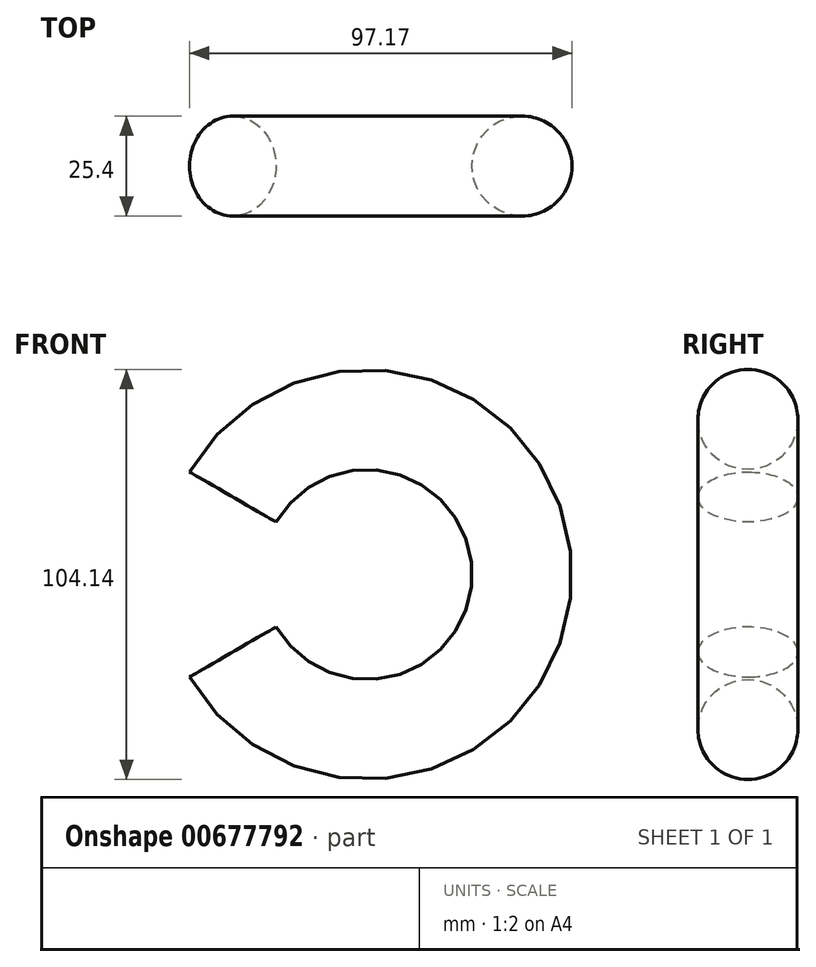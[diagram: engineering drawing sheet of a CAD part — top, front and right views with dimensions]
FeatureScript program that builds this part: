
annotation { "Feature Type Name" : "Feature", "Feature Type Description" : "" }
export const myFeature = defineFeature(function(context is Context, id is Id, definition is map)
    precondition{}
    {
        {
            var Q0;
            Q0=qCreatedBy(makeId("Top.planeOp"),FACE);
            var sketch = newSketch(context, id + "F0", { "sketchPlane" : qUnion([Q0])});
            skLineSegment(sketch, "E0", {"start": v(0, 0) * mm, "end": v(39.37, 0) * mm});
            skCircle(sketch, "E1", {"center": v(39.37, 0) * mm, "radius": 12.7 * mm});
            skLineSegment(sketch, "E2", {"start": v(0, 0) * mm, "end": v(0, 38.92) * mm});
            skSolve(sketch);
        }
        {
            var Q0;
            Q0=makeQuery(id+"F0.imprint","IMPRINT",FACE,{"disambiguationData":[TD([[makeQuery(id+"F0.imprint","IMPRINT",EDGE,{"derivedFrom":sQuery(id+"F0.wireOp",EDGE,"E1")}),1.0]])]});
            var Q1;
            Q1=sQuery(id+"F0.wireOp",EDGE,"E2");
            revolve(context, id + "F1", {"entities" : qUnion([Q0]), "axis" : qUnion([Q1]), "revolveType" : RevolveType.SYMMETRIC, "angle" : 300 * degree});
        }
    });
